# Revit family: PRD_FrankeWS_ShwrFttngsPckg_WallArm_ZAQUA033
name_source: partatom
category: Specialty Equipment
revit_build: Autodesk Revit 2018 (Build: 20190510_1515(x64)
units: mm (PartAtom-declared; Revit-internal decimal feet)

## family parameters
Always vertical = Yes
Cut with Voids When Loaded = Yes
OmniClass Number = 23.45.55.11
OmniClass Title = Sanitary Components
Part Type = Normal
Room Calculation Point = No
Round Connector Dimension = Use Diameter
Shared = No
Work Plane-Based = No

## types (1)
- ZAQUA033
    AssetType = Fixed
    BIMObjectName = PRD_AR_ShowerFittingsPackage_WallArm_ZAQUA033
    BodyMaterial = PRD_AR_ChromatedBrass_HighPolished
    Category = Pr_40_20_87_75, Shower fittings package
    Description = Wall arm with fixed wall flange, polished chromium-plated brass, connections G 1/2 B on both sides, projection 85 mm.
    DurationUnit = year
    Features = polished chrome-plated brass
    Finish = polished chromium-plated
    GrossWeight = 0.50 kg
    IfcExportAs = IfcSanitaryTerminalType
    IfcExportType = USERDEFINED
    InletSize = DN 15
    Manufacturer = KWC Group AG
    ManufacturerName = KWC Group AG
    ManufacturerURL = www.kwc.com
    Material = brass
    Model = ZAQUA033
    ModelNumber = 2000100914
    ModelReference = ZAQUA033
    NBSDescription = Shower fittings package
    NBSReference = 45-35-70/330
    Name = Wall arm ZAQUA033
    NetWeight = 0.49 kg
    NominalDepth = 0 mm  [stored 0 ft]
    NominalHeight = 0 mm  [stored 0 ft]
    NominalLength = 0 mm  [stored 0 ft]
    NominalWidth = 0 mm  [stored 0 ft]
    ProductCode = 210.0574.298
    ProductInformation = https://pim.kwc.com
    Status = New
    TailorMade = No
    Type = Cantilever
    TypeOfConnection = Wall connection
    URL = www.kwc.com
    Uniclass2015Code = Pr_40_20_87_75
    Uniclass2015Title = Shower fittings package
    Uniclass2015Version = Products v1.23
    Version = 1
    WarrantyDurationUnit = year

note: [stored X ft] marks values corroborated as IEEE doubles in the binary element streams (Revit-internal decimal feet)

## geometry (parser evidence)
native form markers: Sweep x3
no freeform markers — native parametric forms only
